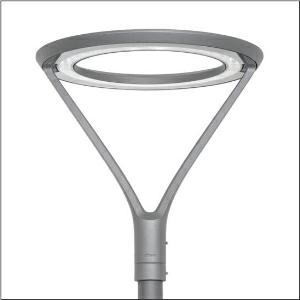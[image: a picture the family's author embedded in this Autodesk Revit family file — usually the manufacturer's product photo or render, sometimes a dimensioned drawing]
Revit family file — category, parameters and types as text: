
# Revit family: dl_r__20___pl1_2s_5xa512832s008p_c84b
name_source: partatom
category: Lighting Fixtures
units: mm (PartAtom-declared; Revit-internal decimal feet)

## family parameters
Cut with Voids When Loaded = No
Host = Face
Light Source = No
Part Type = Normal
Room Calculation Point = No
Round Connector Dimension = Use Diameter
Shared = No

## types (1)
- --- (1 x LED, 4250 lm, 43.6 W, 2200K)
    Apparent Load = 44 VA
    CIE Flux Codes = 33 78 99 100 100
    Color Rendering = 70
    Color Temperature = 2200K
    Default Elevation = 1800 mm
    Description = DL® 20, mast luminaire, primary light control with reflector, highly specular, primary optical cover: cover, of toughened safety glass of clear glass with excellent transmission level, light distribution: PL1.2s, light emission: direct distribution, primary light characteristic: symmetric, installation type: post-top, LED, High Power LED, rated luminous flux: 4.210lm, luminous efficacy: 80lm/W, light colour: 722, colour temperature: 2200K, control gear: ECG Plus, control: flexible luminous flux parameterisation, time-dependent luminous flux control, constant luminous flux control, digital communication interface, power reduction, overheat protection, electronic power reduction, mains connection: 230..240V, 50/60Hz, connection cable pre-assembled, cable length: 5m, start of lifetime: 53W, end of service life: 54W, reduction: 24W, luminaire housing, upper part, of cast aluminium, powder-coated, Siteco® metallic grey (DB 702S), diameter: 690mm, height: 690mm, spigot size: 76mm (post-top), luminaire housing, of cast aluminium, powder-coated, Siteco® metallic grey (DB 702S), equipment: Power, protection rating (complete): IP66, insulation class (complete): insulation class II (safety insulation), certification: CE, ENEC, VDE, impact resistance: IK08, permissible operating ambient temperature: -25..+30°C, standard-compliant lighting for roads and squares, packaging unit: 1 piece

Light Distribution: PL1.2s
    Height = 690 mm
    Lamp = 1 x LED
    Lamp Light Flux = 4250 lm
    Lamp Power = 43.6 W
    Lamp count = 1
    Length = 690 mm
    Luminous efficacy = 97 lm/W
    Manufacturer = Siteco
    ModVariant = No
    Model = 5XA512832S008P
    Number of Poles = 1
    OnlyDefault = Yes
    Power Factor = 1
    Product Name = DL® 20 | PL1.2s
    Product group = mast luminaire | pylon top
    ProductGroupID = 6100
    Protection Class = Protection class II
    Protection Degree = IP 66
    RLX_Detail_Level = 1
    RLX_Emergency_Light_Flux = 0 lm
    RLX_Emergency_Type = 0
    RLX_Emergency_Type_DB = No
    RlxData = <blob elided: 204033 chars, md5=d6c3deda>
    Socket = socket
    Standby Power = 0 W
    System Light Flux = 4250 lm
    System Power = 44 W
    Type Comments = factory setting: luminous flux: 100 % | dim-lin: 254 | 587 mA
    Type Image = l_1006001.jpg
    URL = http://relux.com
    VarID = @adj_028055
    Voltage = 0 V
    Weight = 0.00 kg
    Width = 0 mm  [stored 0 ft]

note: [stored X ft] marks values corroborated as IEEE doubles in the binary element streams (Revit-internal decimal feet)

## geometry (parser evidence)
native form markers: Blend x4, Sweep x9
no freeform markers — native parametric forms only
